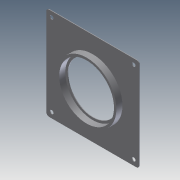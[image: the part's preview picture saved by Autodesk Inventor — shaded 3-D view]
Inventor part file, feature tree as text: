
AUTODESK INVENTOR PART (.ipt)
format: ipt  version: 2011 (Build 150239000, 239)  size: 146,944 bytes
history: native  units: in
note: dims shown in document units (in); Inventor stores cm internally (conversion verified against a paired STEP export)
features: extrude x7, sketch x7, fillet x1
ambient origin geometry x8: Origin, YZ Plane, XZ Plane, XY Plane, X Axis, Y Axis, Z Axis, Center Point
bodies: Solid1 (feature_tree)
feature tree (15):
  extrude  "Extrusion1"  Depth=4.0in
  extrude  "Extrusion2"  Depth=2.16in
  extrude  "Extrusion3"  Depth=1.7655in
  extrude  "Extrusion4"  Depth=0.029in TaperAngle=0.0deg
  extrude  "Extrusion5"  Depth=2.36in
  fillet  "Fillet1"  Radius=2.56in
  extrude  "Extrusion6"  Depth=0.125in
  extrude  "Extrusion7"  Depth=0.235in
  sketch  "Sketch1"  dims[d0=4.0in d1=4.0in]
  sketch  "Sketch2"  dims[d2=0.029in d3=0.0in d4=2.16in]
  sketch  "Sketch3"  dims[d5=0.029in d6=0.0in d7=1.7655in]
  sketch  "Sketch4"  dims[d8=0.156in d9=0.029in d10=0.0in]
  sketch  "Sketch5"  dims[d11=0.029in d12=0.0in d13=2.36in d14=2.56in]
  sketch  "Sketch6"  dims[d15=0.262in d16=0.0in d17=0.125in]
  sketch  "Sketch7"  dims[d18=0.029in d19=0.0in d20=0.235in d21=0.235in d22=0.235in d23=0.235in d24=0.235in d25=0.156in d26=0.029in d27=0.0in]
